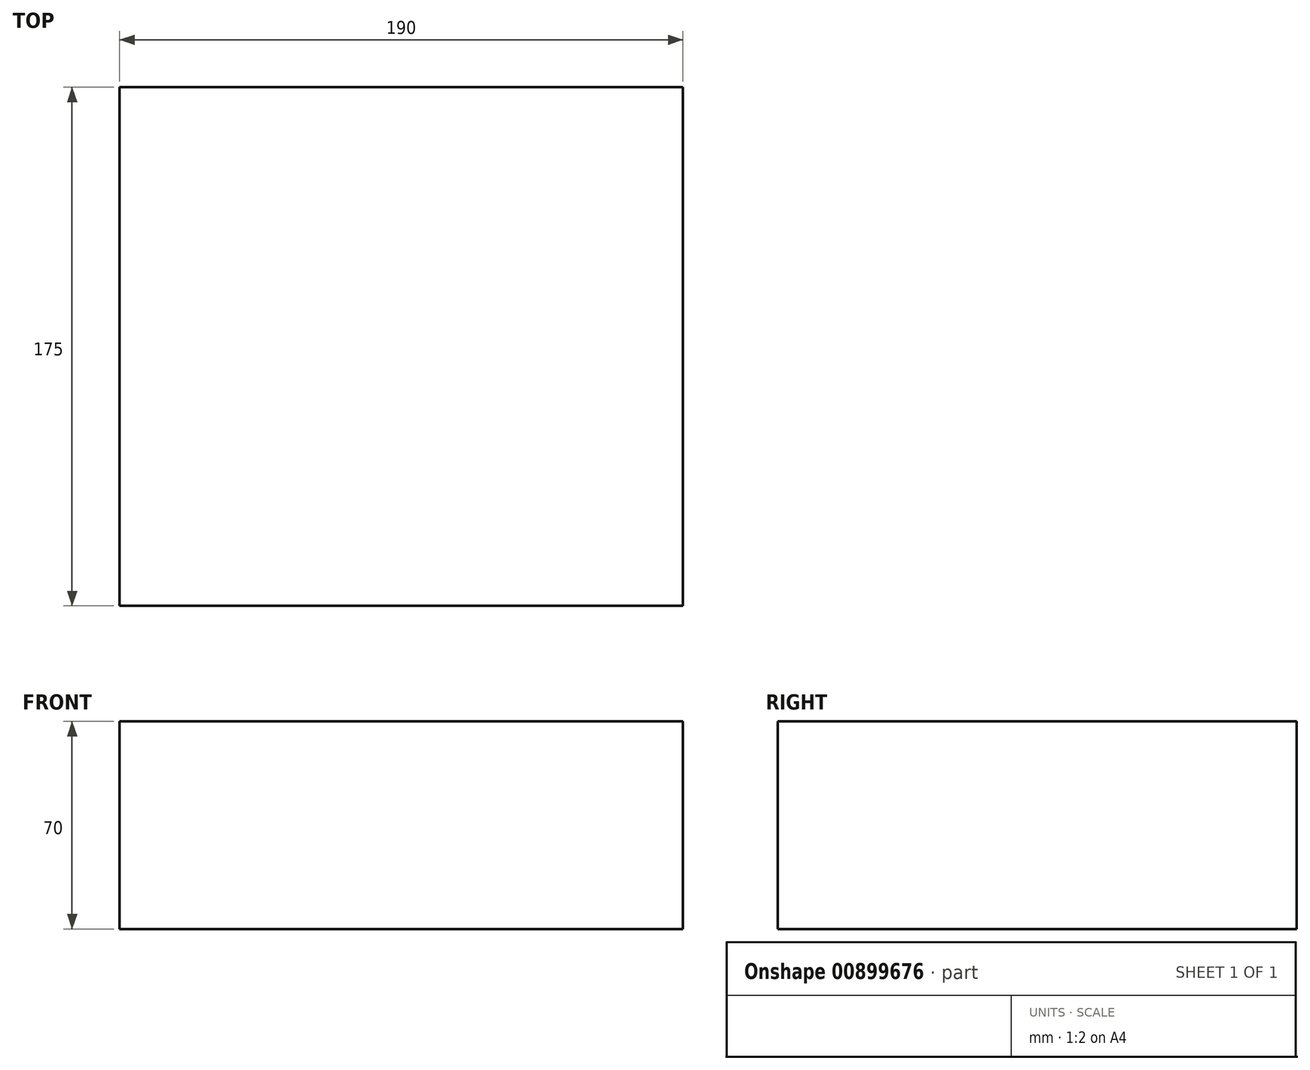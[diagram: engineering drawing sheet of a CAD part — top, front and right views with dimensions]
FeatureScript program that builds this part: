
annotation { "Feature Type Name" : "Feature", "Feature Type Description" : "" }
export const myFeature = defineFeature(function(context is Context, id is Id, definition is map)
    precondition{}
    {
        {
            var Q0;
            Q0=qCreatedBy(makeId("Top.planeOp"),FACE);
            var sketch = newSketch(context, id + "F0", { "sketchPlane" : qUnion([Q0])});
            skLineSegment(sketch, "E0.bottom", {"start": v(-95, -87.5) * mm, "end": v(95, -87.5) * mm});
            skLineSegment(sketch, "E0.top", {"start": v(-95, 87.5) * mm, "end": v(95, 87.5) * mm});
            skLineSegment(sketch, "E0.left", {"start": v(-95, -87.5) * mm, "end": v(-95, 87.5) * mm});
            skLineSegment(sketch, "E0.right", {"start": v(95, -87.5) * mm, "end": v(95, 87.5) * mm});
            skPoint(sketch, "E0.middle", {"position": v(0, 0) * mm});
            skSolve(sketch);
        }
        {
            var Q0;
            Q0=makeQuery(id+"F0.imprint","IMPRINT",FACE,{"disambiguationData":[TD([[makeQuery(id+"F0.imprint","IMPRINT",EDGE,{"derivedFrom":sQuery(id+"F0.wireOp",EDGE,"E0.bottom")}),1.0]])]});
            var Q1;
            Q1 = qSketchRegion(id + "F0", true);
            extrude(context, id + "F1", {"entities" : qUnion([Q0, Q1]), "depth" : 70 * mm, "offsetDistance" : 25 * mm});
        }
    });
